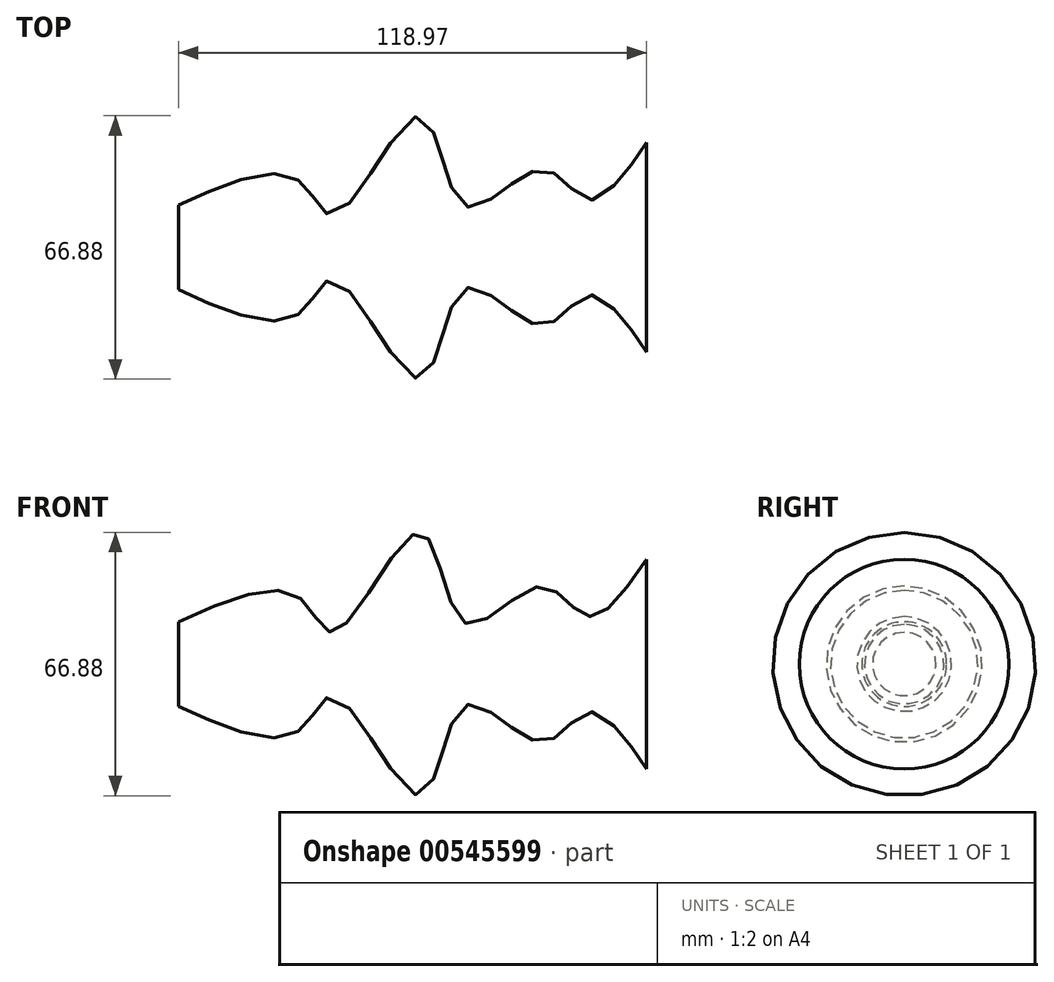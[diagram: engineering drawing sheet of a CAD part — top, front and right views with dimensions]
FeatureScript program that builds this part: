
annotation { "Feature Type Name" : "Feature", "Feature Type Description" : "" }
export const myFeature = defineFeature(function(context is Context, id is Id, definition is map)
    precondition{}
    {
        {
            var Q0;
            Q0=qCreatedBy(makeId("Top.planeOp"),FACE);
            var sketch = newSketch(context, id + "F0", { "sketchPlane" : qUnion([Q0])});
            skFitSpline(sketch, "E0", {"points": [v(-67.7, 10.76) * mm, v(-37.1, 17) * mm, v(-27.76, 8.21) * mm, v(-6.23, 33.43) * mm, v(5.1, 10.48) * mm, v(24.36, 19.83) * mm, v(35.98, 12.18) * mm, v(51.27, 26.63) * mm], "startDerivative": vector(214.08, 96.08) * mm, "endDerivative": vector(115.79, 168.59) * mm});
            skLineSegment(sketch, "E1", {"start": v(51.27, 26.63) * mm, "end": v(51.27, 0) * mm});
            skLineSegment(sketch, "E2", {"start": v(-67.7, 10.76) * mm, "end": v(-67.7, 0) * mm});
            skLineSegment(sketch, "E3", {"start": v(-67.7, 0) * mm, "end": v(51.27, 0) * mm});
            skSolve(sketch);
        }
        {
            var Q0;
            Q0=makeQuery(id+"F0.imprint","IMPRINT",FACE,{"disambiguationData":[TD([[makeQuery(id+"F0.imprint","IMPRINT",EDGE,{"derivedFrom":sQuery(id+"F0.wireOp",EDGE,"E0")}),-1.0]])]});
            var Q1;
            Q1=sQuery(id+"F0.wireOp",EDGE,"E3");
            revolve(context, id + "F1", {"entities" : qUnion([Q0]), "axis" : qUnion([Q1]), "revolveType" : RevolveType.FULL});
        }
    });
